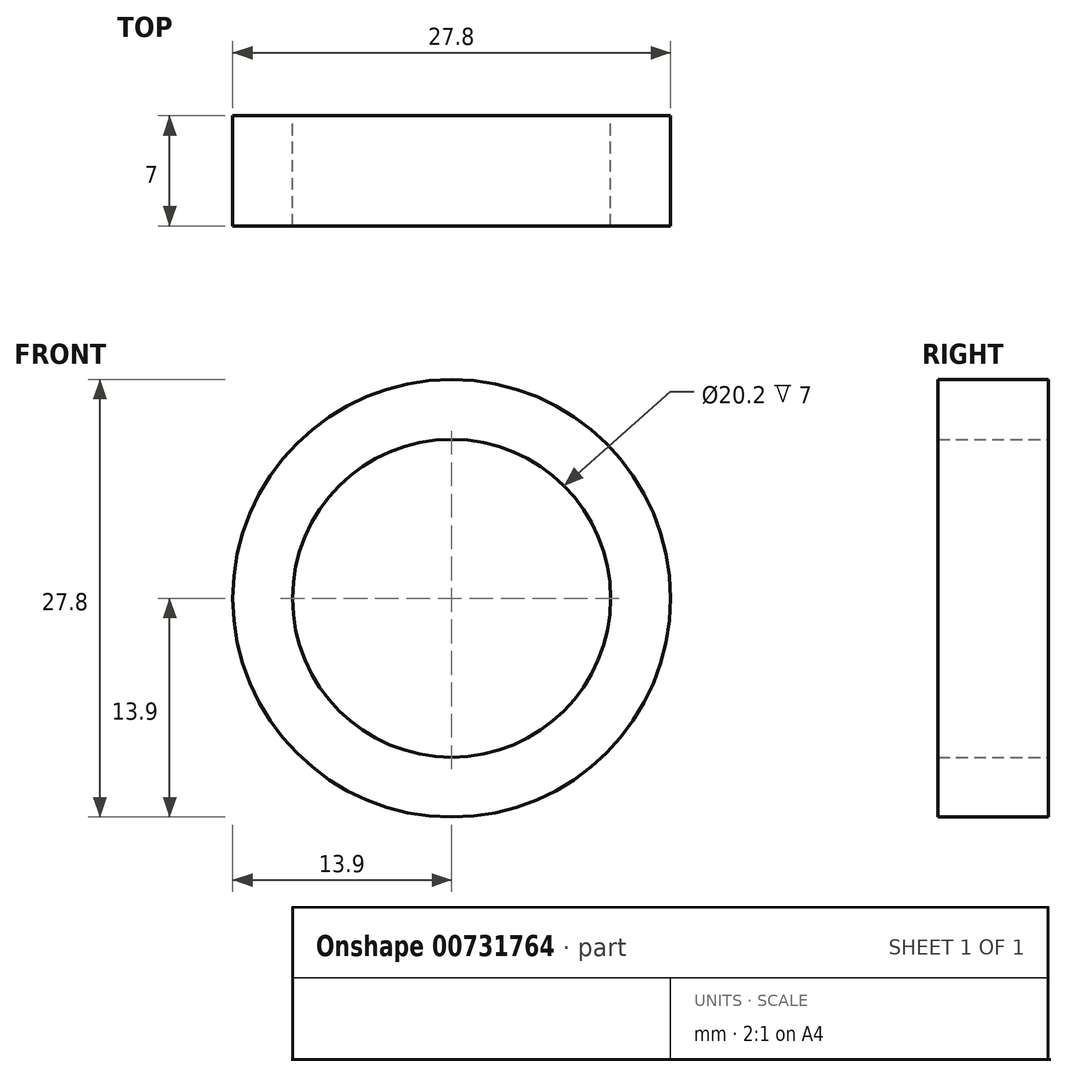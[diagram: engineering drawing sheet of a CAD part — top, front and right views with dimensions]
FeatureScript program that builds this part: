
annotation { "Feature Type Name" : "Feature", "Feature Type Description" : "" }
export const myFeature = defineFeature(function(context is Context, id is Id, definition is map)
    precondition{}
    {
        {
            var Q0;
            Q0=qCreatedBy(makeId("Front.planeOp"),FACE);
            var sketch = newSketch(context, id + "F0", { "sketchPlane" : qUnion([Q0])});
            skCircle(sketch, "E0", {"center": v(0, 0) * mm, "radius": 10.1 * mm});
            skCircle(sketch, "E1", {"center": v(0, 0) * mm, "radius": 13.9 * mm});
            skSolve(sketch);
        }
        {
            var Q0;
            Q0 = qSketchRegion(id + "F0", true);
            extrude(context, id + "F1", {"entities" : qUnion([Q0]), "depth" : 7 * mm, "offsetDistance" : 25 * mm});
        }
    });
